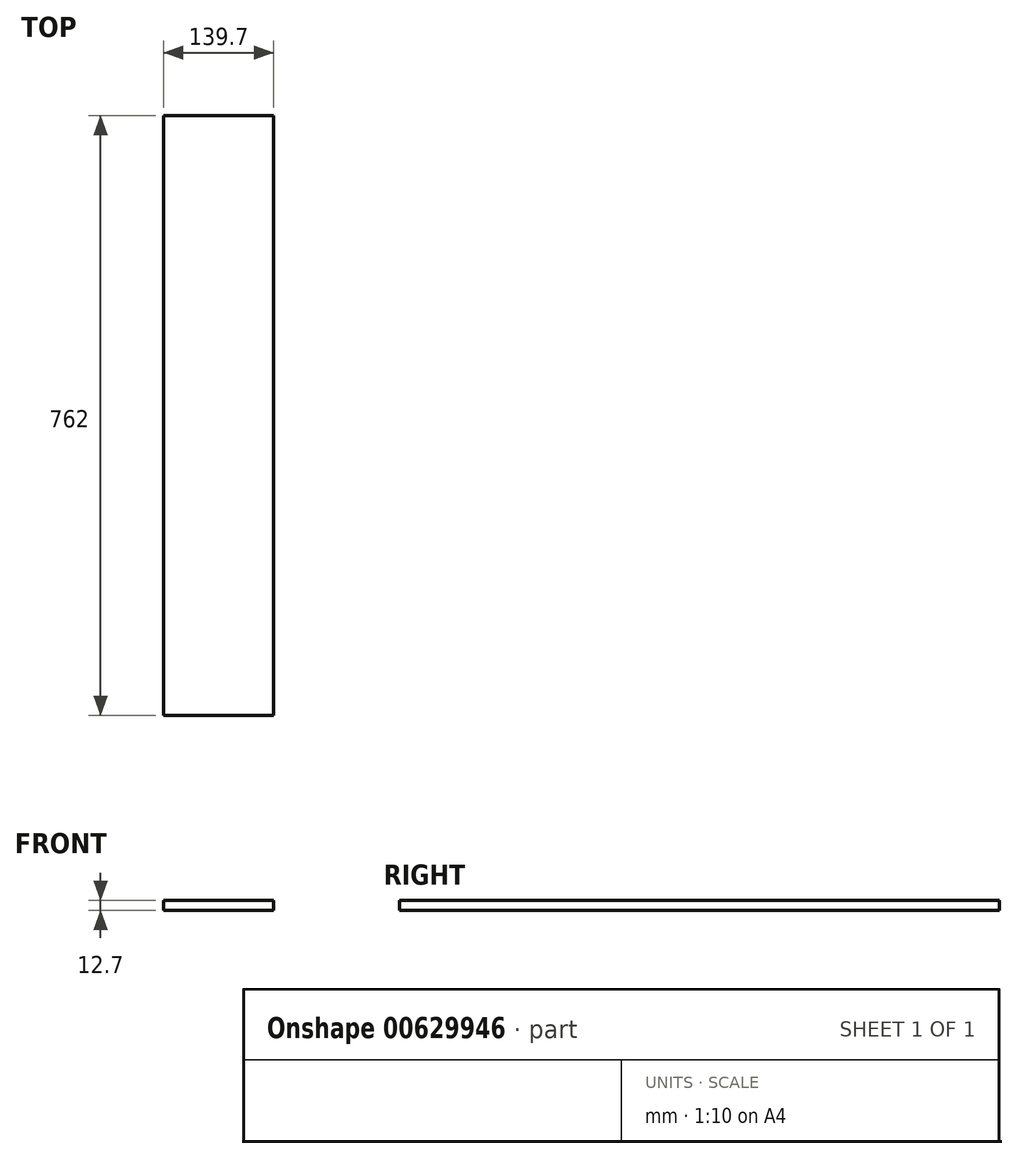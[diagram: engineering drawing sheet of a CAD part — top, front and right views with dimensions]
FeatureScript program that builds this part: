
annotation { "Feature Type Name" : "Feature", "Feature Type Description" : "" }
export const myFeature = defineFeature(function(context is Context, id is Id, definition is map)
    precondition{}
    {
        {
            var Q0;
            Q0=qCreatedBy(makeId("Front.planeOp"),FACE);
            var sketch = newSketch(context, id + "F0", { "sketchPlane" : qUnion([Q0])});
            skLineSegment(sketch, "E0.bottom", {"start": v(-71, -15.52) * mm, "end": v(68.7, -15.52) * mm});
            skLineSegment(sketch, "E0.top", {"start": v(-71, -28.22) * mm, "end": v(68.7, -28.22) * mm});
            skLineSegment(sketch, "E0.left", {"start": v(-71, -15.52) * mm, "end": v(-71, -28.22) * mm});
            skLineSegment(sketch, "E0.right", {"start": v(68.7, -15.52) * mm, "end": v(68.7, -28.22) * mm});
            skSolve(sketch);
        }
        {
            var Q0;
            Q0 = qSketchRegion(id + "F0", true);
            extrude(context, id + "F1", {"entities" : qUnion([Q0]), "depth" : 762 * mm, "offsetDistance" : 25.4 * mm});
        }
    });
